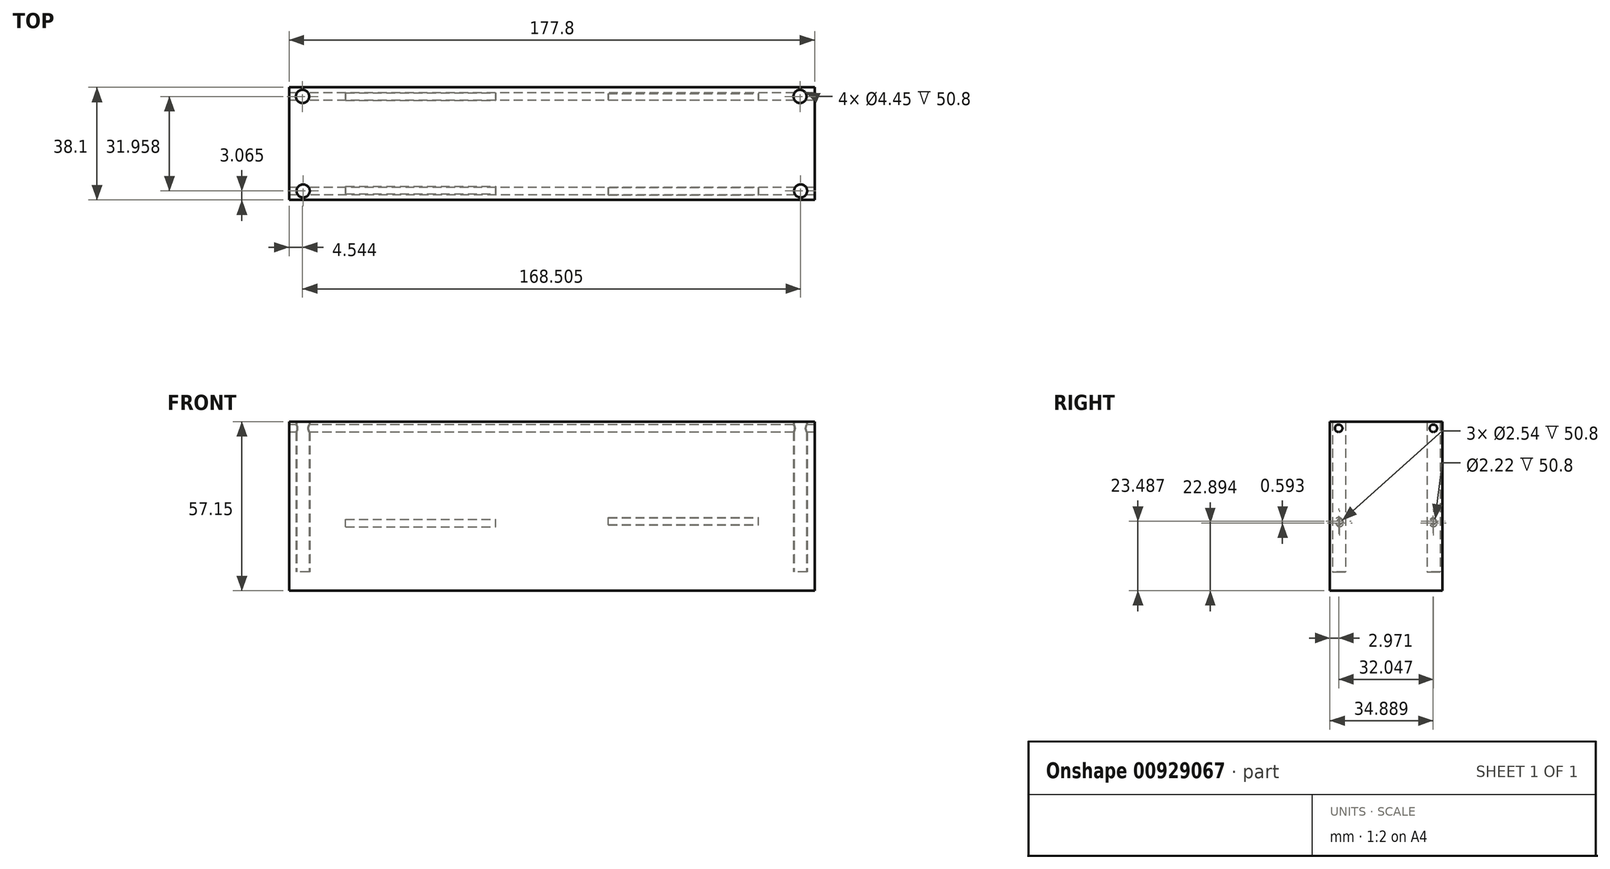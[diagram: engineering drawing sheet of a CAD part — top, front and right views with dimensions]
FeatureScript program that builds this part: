
annotation { "Feature Type Name" : "Feature", "Feature Type Description" : "" }
export const myFeature = defineFeature(function(context is Context, id is Id, definition is map)
    precondition{}
    {
        {
            var Q0;
            Q0=qCreatedBy(makeId("Top.planeOp"),FACE);
            var sketch = newSketch(context, id + "F0", { "sketchPlane" : qUnion([Q0])});
            skLineSegment(sketch, "E0.bottom", {"start": v(-97.84, -32.3) * mm, "end": v(79.96, -32.3) * mm});
            skLineSegment(sketch, "E0.top", {"start": v(-97.84, 5.8) * mm, "end": v(79.96, 5.8) * mm});
            skLineSegment(sketch, "E0.left", {"start": v(-97.84, -32.3) * mm, "end": v(-97.84, 5.8) * mm});
            skLineSegment(sketch, "E0.right", {"start": v(79.96, -32.3) * mm, "end": v(79.96, 5.8) * mm});
            skSolve(sketch);
        }
        {
            var Q0;
            Q0=makeQuery(id+"F0.imprint","IMPRINT",FACE,{"disambiguationData":[TD([[makeQuery(id+"F0.imprint","IMPRINT",EDGE,{"derivedFrom":sQuery(id+"F0.wireOp",EDGE,"E0.bottom")}),1.0]])]});
            extrude(context, id + "F1", {"entities" : qUnion([Q0]), "depth" : 6.35 * mm, "offsetDistance" : 25.4 * mm});
        }
        {
            var Q0;
            Q0=makeQuery(id+"F1.opExtrude","CAP_FACE",FACE,{"disambiguationData":[OSD([sQuery(id+"F0.wireOp",EDGE,"E0.bottom"),sQuery(id+"F0.wireOp",EDGE,"E0.top"),sQuery(id+"F0.wireOp",EDGE,"E0.left"),sQuery(id+"F0.wireOp",EDGE,"E0.right")])],"isStart":false});
            var sketch = newSketch(context, id + "F2", { "sketchPlane" : qUnion([Q0])});
            skLineSegment(sketch, "E1", {"start": v(-97.84, -13.26) * mm, "end": v(-8.94, -13.26) * mm, "construction": true});
            skPoint(sketch, "E1.endSnap0", {"position": v(-8.94, -32.3) * mm});
            skCircle(sketch, "E2", {"center": v(-8.94, -13.26) * mm, "radius": 7.62 * mm});
            skSolve(sketch);
        }
        {
            var Q0;
            Q0=makeQuery(id+"F1.opExtrude","CAP_FACE",FACE,{"disambiguationData":[OSD([sQuery(id+"F0.wireOp",EDGE,"E0.bottom"),sQuery(id+"F0.wireOp",EDGE,"E0.top"),sQuery(id+"F0.wireOp",EDGE,"E0.left"),sQuery(id+"F0.wireOp",EDGE,"E0.right")])],"isStart":false});
            var sketch = newSketch(context, id + "F3", { "sketchPlane" : qUnion([Q0])});
            skCircle(sketch, "E3", {"center": v(-8.94, -29.25) * mm, "radius": 2.22 * mm});
            skCircle(sketch, "E4", {"center": v(-8.73, 2.71) * mm, "radius": 2.22 * mm});
            skLineSegment(sketch, "E5", {"start": v(33.13, 2.71) * mm, "end": v(33.13, 5.8) * mm, "construction": true});
            skLineSegment(sketch, "E6", {"start": v(33.13, 5.8) * mm, "end": v(33.13, -32.3) * mm, "construction": true});
            skCircle(sketch, "E7.MirrorC", {"center": v(75, 2.71) * mm, "radius": 2.22 * mm});
            skCircle(sketch, "E8.MirrorC", {"center": v(75.2, -29.25) * mm, "radius": 2.22 * mm});
            skLineSegment(sketch, "E9", {"start": v(-51.01, 5.8) * mm, "end": v(-51.01, -32.3) * mm, "construction": true});
            skLineSegment(sketch, "E10", {"start": v(-51.01, -32.3) * mm, "end": v(-8.53, -13.26) * mm, "construction": true});
            skPoint(sketch, "E10.endSnap0", {"position": v(-21.64, -13.26) * mm});
            skLineSegment(sketch, "E11", {"start": v(33.13, -32.3) * mm, "end": v(-8.53, -13.26) * mm, "construction": true});
            skCircle(sketch, "E12.MirrorC", {"center": v(-93.3, 2.71) * mm, "radius": 2.22 * mm});
            skCircle(sketch, "E13.MirrorC", {"center": v(-93.09, -29.25) * mm, "radius": 2.22 * mm});
            skPoint(sketch, "E14", {"position": v(-8.94, -32.3) * mm});
            skSolve(sketch);
        }
        {
            var Q0;
            Q0=makeQuery(id+"F3.imprint","IMPRINT",FACE,{"disambiguationData":[TD([[makeQuery(id+"F3.imprint","IMPRINT",EDGE,{"derivedFrom":sQuery(id+"F3.wireOp",EDGE,"E4")}),1.0]])]});
            var Q1;
            Q1=makeQuery(id+"F3.imprint","IMPRINT",FACE,{"disambiguationData":[TD([[makeQuery(id+"F3.imprint","IMPRINT",EDGE,{"derivedFrom":sQuery(id+"F3.wireOp",EDGE,"E3")}),1.0]])]});
            var Q2;
            Q2=makeQuery(id+"F3.imprint","IMPRINT",FACE,{"disambiguationData":[TD([[makeQuery(id+"F3.imprint","IMPRINT",EDGE,{"derivedFrom":sQuery(id+"F3.wireOp",EDGE,"E12.MirrorC")}),-1.0]])]});
            var Q3;
            Q3=makeQuery(id+"F3.imprint","IMPRINT",FACE,{"disambiguationData":[TD([[makeQuery(id+"F3.imprint","IMPRINT",EDGE,{"derivedFrom":sQuery(id+"F3.wireOp",EDGE,"E13.MirrorC")}),-1.0]])]});
            var Q4;
            Q4=makeQuery(id+"F3.imprint","IMPRINT",FACE,{"disambiguationData":[TD([[makeQuery(id+"F3.imprint","IMPRINT",EDGE,{"derivedFrom":sQuery(id+"F3.wireOp",EDGE,"E7.MirrorC")}),-1.0]])]});
            var Q5;
            Q5=makeQuery(id+"F3.imprint","IMPRINT",FACE,{"disambiguationData":[TD([[makeQuery(id+"F3.imprint","IMPRINT",EDGE,{"derivedFrom":sQuery(id+"F3.wireOp",EDGE,"E8.MirrorC")}),-1.0]])]});
            extrude(context, id + "F4", {"entities" : qUnion([Q0, Q1, Q2, Q3, Q4, Q5]), "operationType" : NewBodyOperationType.ADD, "depth" : 50.8 * mm, "offsetDistance" : 25.4 * mm});
        }
        {
            var Q0;
            Q0=makeQuery(id+"F1.opExtrude","CAP_FACE",FACE,{"disambiguationData":[OSD([sQuery(id+"F0.wireOp",EDGE,"E0.bottom"),sQuery(id+"F0.wireOp",EDGE,"E0.top"),sQuery(id+"F0.wireOp",EDGE,"E0.left"),sQuery(id+"F0.wireOp",EDGE,"E0.right")])],"isStart":false});
            var sketch = newSketch(context, id + "F5", { "sketchPlane" : qUnion([Q0])});
            skLineSegment(sketch, "E15", {"start": v(-21.64, -13.33) * mm, "end": v(-97.84, -13.26) * mm, "construction": true});
            skPoint(sketch, "E15.endSnap0", {"position": v(-97.84, -13.26) * mm});
            skLineSegment(sketch, "E16", {"start": v(-8.73, 2.71) * mm, "end": v(-53.32, 2.71) * mm, "construction": true});
            skCircle(sketch, "E17", {"center": v(-53.32, 2.71) * mm, "radius": 1.9 * mm});
            skCircle(sketch, "E18.MirrorC", {"center": v(-53.35, -29.31) * mm, "radius": 1.9 * mm});
            skLineSegment(sketch, "E19", {"start": v(-8.73, 5.8) * mm, "end": v(-8.73, -32.3) * mm, "construction": true});
            skCircle(sketch, "E20.MirrorC", {"center": v(35.86, 2.71) * mm, "radius": 1.9 * mm});
            skCircle(sketch, "E21.MirrorC", {"center": v(35.89, -29.31) * mm, "radius": 1.9 * mm});
            skLineSegment(sketch, "E22", {"start": v(-53.17, 5.8) * mm, "end": v(-53.17, -32.3) * mm, "construction": true});
            skLineSegment(sketch, "E23", {"start": v(35.86, 5.8) * mm, "end": v(35.86, -32.3) * mm, "construction": true});
            skSolve(sketch);
        }
        {
            var Q0;
            Q0=makeQuery(id+"F5.imprint","IMPRINT",FACE,{"disambiguationData":[TD([[makeQuery(id+"F5.imprint","IMPRINT",EDGE,{"derivedFrom":sQuery(id+"F5.wireOp",EDGE,"E17")}),1.0]])]});
            var Q1;
            Q1=makeQuery(id+"F5.imprint","IMPRINT",FACE,{"disambiguationData":[TD([[makeQuery(id+"F5.imprint","IMPRINT",EDGE,{"derivedFrom":sQuery(id+"F5.wireOp",EDGE,"E18.MirrorC")}),-1.0]])]});
            var Q2;
            Q2=makeQuery(id+"F5.imprint","IMPRINT",FACE,{"disambiguationData":[TD([[makeQuery(id+"F5.imprint","IMPRINT",EDGE,{"derivedFrom":sQuery(id+"F5.wireOp",EDGE,"E20.MirrorC")}),-1.0]])]});
            var Q3;
            Q3=makeQuery(id+"F5.imprint","IMPRINT",FACE,{"disambiguationData":[TD([[makeQuery(id+"F5.imprint","IMPRINT",EDGE,{"derivedFrom":sQuery(id+"F5.wireOp",EDGE,"E21.MirrorC")}),1.0]])]});
            extrude(context, id + "F6", {"entities" : qUnion([Q0, Q1, Q2, Q3]), "operationType" : NewBodyOperationType.ADD, "depth" : 19.05 * mm, "offsetDistance" : 25.4 * mm});
        }
        {
            var Q0;
            Q0=qCreatedBy(makeId("Right.planeOp"),FACE);
            cPlane(context, id + "F7", {"entities" : qUnion([Q0]), "cplaneType" : CPlaneType.OFFSET, "offset" : 8.9 * mm, "oppositeDirection" : true, "width" : 152.4 * mm, "height" : 152.4 * mm});
        }
        {
            var Q0;
            Q0=qCreatedBy(id+"F7.planeOp",FACE);
            var sketch = newSketch(context, id + "F8", { "sketchPlane" : qUnion([Q0])});
            skCircle(sketch, "E24", {"center": v(-29.35, 54.92) * mm, "radius": 1.27 * mm});
            skLineSegment(sketch, "E25", {"start": v(-29.35, 54.92) * mm, "end": v(2.69, 54.92) * mm, "construction": true});
            skCircle(sketch, "E26", {"center": v(2.69, 54.92) * mm, "radius": 1.27 * mm});
            skSolve(sketch);
        }
        {
            var Q0;
            Q0=makeQuery(id+"F8.imprint","IMPRINT",FACE,{"disambiguationData":[TD([[makeQuery(id+"F8.imprint","IMPRINT",EDGE,{"derivedFrom":sQuery(id+"F8.wireOp",EDGE,"E26")}),1.0]])]});
            var Q1;
            Q1=makeQuery(id+"F8.imprint","IMPRINT",FACE,{"disambiguationData":[TD([[makeQuery(id+"F8.imprint","IMPRINT",EDGE,{"derivedFrom":sQuery(id+"F8.wireOp",EDGE,"E24")}),1.0]])]});
            extrude(context, id + "F9", {"entities" : qUnion([Q0, Q1]), "operationType" : NewBodyOperationType.REMOVE, "endBound" : BoundingType.THROUGH_ALL, "depth" : 25.4 * mm, "offsetDistance" : 25.4 * mm, "hasSecondDirection" : true, "secondDirectionBound" : SecondDirectionBoundingType.THROUGH_ALL, "secondDirectionOppositeDirection" : true, "secondDirectionDepth" : 25.4 * mm});
        }
        {
            var Q0;
            Q0=qCreatedBy(id+"F7.planeOp",FACE);
            cPlane(context, id + "F10", {"entities" : qUnion([Q0]), "cplaneType" : CPlaneType.OFFSET, "offset" : 44.45 * mm, "width" : 152.4 * mm, "height" : 152.4 * mm});
        }
        {
            var Q0;
            Q0=qCreatedBy(id+"F10.planeOp",FACE);
            var sketch = newSketch(context, id + "F11", { "sketchPlane" : qUnion([Q0])});
            skLineSegment(sketch, "E27", {"start": v(2.58, 23.49) * mm, "end": v(-29.34, 23.49) * mm, "construction": true});
            skLineSegment(sketch, "E28", {"start": v(-29.34, 23.49) * mm, "end": v(-29.34, 8.07) * mm, "construction": true});
            skLineSegment(sketch, "E29", {"start": v(-29.34, 8.07) * mm, "end": v(2.58, 8.07) * mm, "construction": true});
            skLineSegment(sketch, "E30", {"start": v(2.58, 8.07) * mm, "end": v(2.58, 23.49) * mm, "construction": true});
            skCircle(sketch, "E31", {"center": v(-29.34, 23.49) * mm, "radius": 1.27 * mm});
            skCircle(sketch, "E32", {"center": v(2.58, 23.49) * mm, "radius": 1.1 * mm});
            skSolve(sketch);
        }
        {
            var Q0;
            Q0=makeQuery(id+"F11.imprint","IMPRINT",FACE,{"disambiguationData":[TD([[makeQuery(id+"F11.imprint","IMPRINT",EDGE,{"derivedFrom":sQuery(id+"F11.wireOp",EDGE,"E31")}),1.0]])]});
            var Q1;
            Q1=makeQuery(id+"F11.imprint","IMPRINT",FACE,{"disambiguationData":[TD([[makeQuery(id+"F11.imprint","IMPRINT",EDGE,{"derivedFrom":sQuery(id+"F11.wireOp",EDGE,"E32")}),1.0]])]});
            extrude(context, id + "F12", {"entities" : qUnion([Q0, Q1]), "operationType" : NewBodyOperationType.REMOVE, "oppositeDirection" : true, "depth" : 25.4 * mm, "offsetDistance" : 25.4 * mm, "hasSecondDirection" : true, "secondDirectionOppositeDirection" : false, "secondDirectionDepth" : 25.4 * mm});
        }
        {
            var Q0;
            Q0=qCreatedBy(id+"F7.planeOp",FACE);
            cPlane(context, id + "F13", {"entities" : qUnion([Q0]), "cplaneType" : CPlaneType.OFFSET, "offset" : 44.45 * mm, "oppositeDirection" : true, "width" : 152.4 * mm, "height" : 152.4 * mm});
        }
        {
            var Q0;
            Q0=qCreatedBy(id+"F13.planeOp",FACE);
            var sketch = newSketch(context, id + "F14", { "sketchPlane" : qUnion([Q0])});
            skLineSegment(sketch, "E33.bottom", {"start": v(2.7, 8.16) * mm, "end": v(-29.01, 8.16) * mm, "construction": true});
            skLineSegment(sketch, "E33.top", {"start": v(2.7, 22.9) * mm, "end": v(-29.01, 22.9) * mm, "construction": true});
            skLineSegment(sketch, "E33.left", {"start": v(2.7, 8.16) * mm, "end": v(2.7, 22.9) * mm, "construction": true});
            skLineSegment(sketch, "E33.right", {"start": v(-29.01, 8.16) * mm, "end": v(-29.01, 22.9) * mm, "construction": true});
            skCircle(sketch, "E34", {"center": v(2.7, 22.9) * mm, "radius": 1.27 * mm});
            skCircle(sketch, "E35", {"center": v(-29.01, 22.9) * mm, "radius": 1.27 * mm});
            skSolve(sketch);
        }
        {
            var Q0;
            Q0=makeQuery(id+"F14.imprint","IMPRINT",FACE,{"disambiguationData":[TD([[makeQuery(id+"F14.imprint","IMPRINT",EDGE,{"derivedFrom":sQuery(id+"F14.wireOp",EDGE,"E34")}),1.0]])]});
            var Q1;
            Q1=makeQuery(id+"F14.imprint","IMPRINT",FACE,{"disambiguationData":[TD([[makeQuery(id+"F14.imprint","IMPRINT",EDGE,{"derivedFrom":sQuery(id+"F14.wireOp",EDGE,"E35")}),1.0]])]});
            extrude(context, id + "F15", {"entities" : qUnion([Q0, Q1]), "operationType" : NewBodyOperationType.REMOVE, "oppositeDirection" : true, "depth" : 25.4 * mm, "offsetDistance" : 25.4 * mm, "hasSecondDirection" : true, "secondDirectionOppositeDirection" : false, "secondDirectionDepth" : 25.4 * mm});
        }
    });
